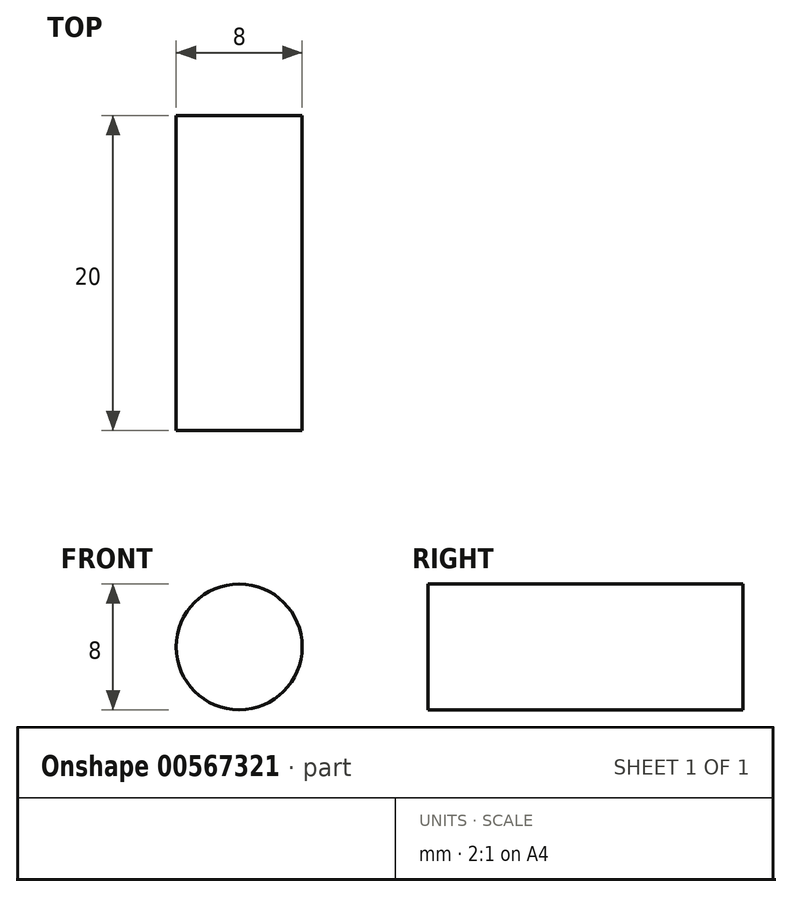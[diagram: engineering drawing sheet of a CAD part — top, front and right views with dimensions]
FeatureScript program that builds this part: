
annotation { "Feature Type Name" : "Feature", "Feature Type Description" : "" }
export const myFeature = defineFeature(function(context is Context, id is Id, definition is map)
    precondition{}
    {
        {
            var Q0;
            Q0=qCreatedBy(makeId("Front.planeOp"),FACE);
            var sketch = newSketch(context, id + "F0", { "sketchPlane" : qUnion([Q0])});
            skCircle(sketch, "E0", {"center": v(-46.33, 32.9) * mm, "radius": 4 * mm});
            skSolve(sketch);
        }
        {
            var Q0;
            Q0 = qSketchRegion(id + "F0", true);
            extrude(context, id + "F1", {"entities" : qUnion([Q0]), "depth" : 20 * mm, "offsetDistance" : 25 * mm});
        }
    });
